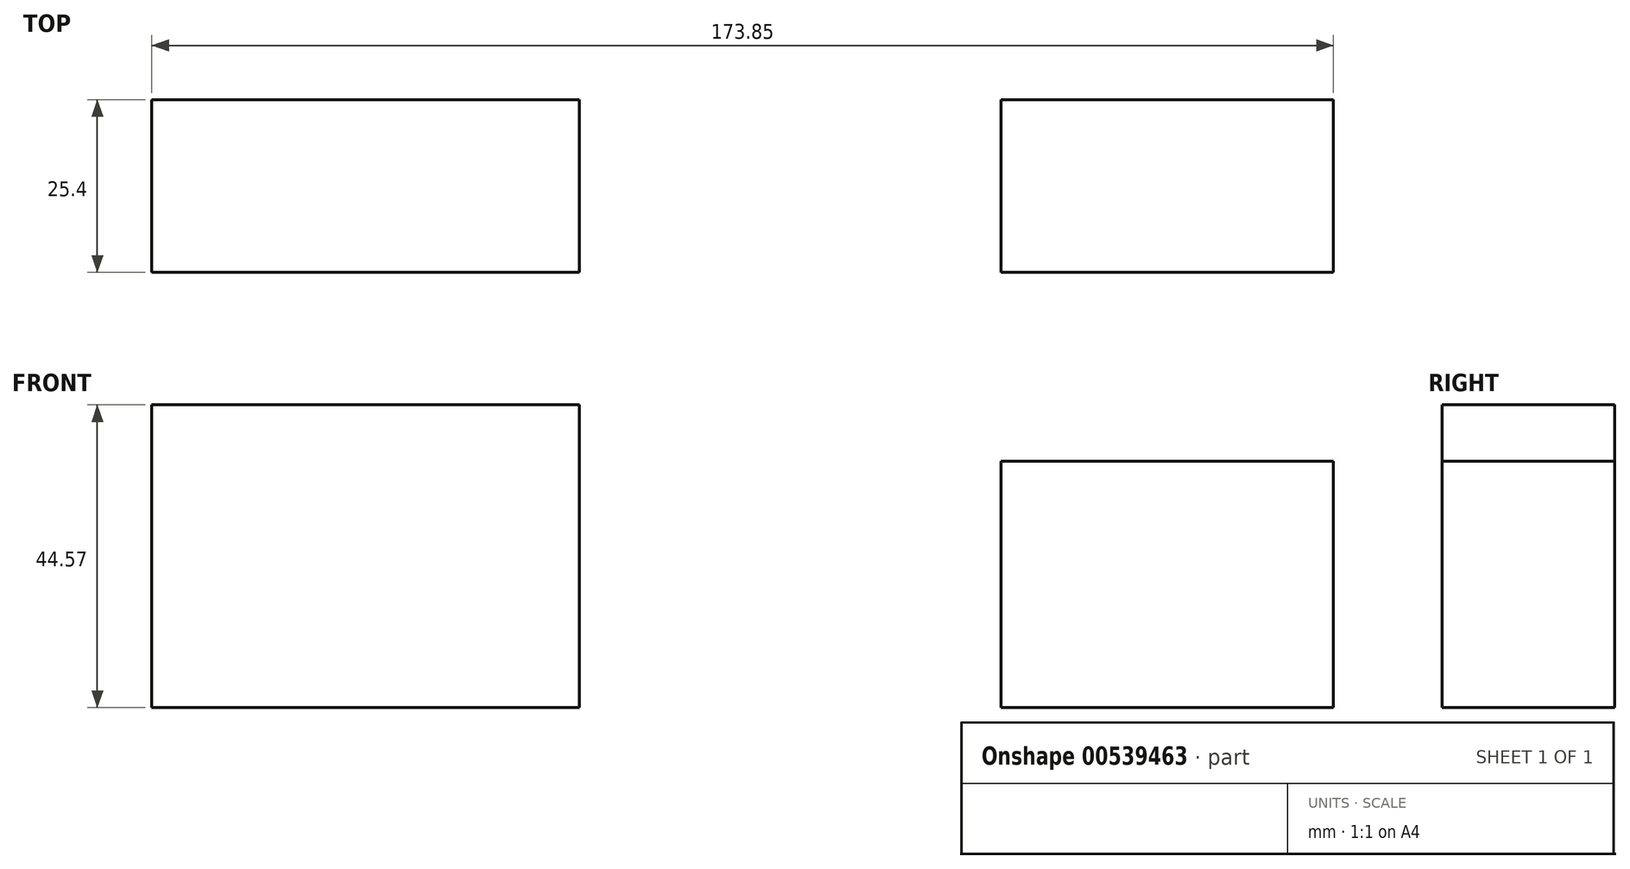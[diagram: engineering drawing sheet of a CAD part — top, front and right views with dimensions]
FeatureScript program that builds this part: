
annotation { "Feature Type Name" : "Feature", "Feature Type Description" : "" }
export const myFeature = defineFeature(function(context is Context, id is Id, definition is map)
    precondition{}
    {
        {
            var Q0;
            Q0=qCreatedBy(makeId("Front.planeOp"),FACE);
            var sketch = newSketch(context, id + "F0", { "sketchPlane" : qUnion([Q0])});
            skLineSegment(sketch, "E0.bottom", {"start": v(-92.4, 44.57) * mm, "end": v(-29.48, 44.57) * mm});
            skLineSegment(sketch, "E0.top", {"start": v(-92.4, 0) * mm, "end": v(-29.48, 0) * mm});
            skLineSegment(sketch, "E0.left", {"start": v(-92.4, 44.57) * mm, "end": v(-92.4, 0) * mm});
            skLineSegment(sketch, "E0.right", {"start": v(-29.48, 44.57) * mm, "end": v(-29.48, 0) * mm});
            skLineSegment(sketch, "E1.bottom", {"start": v(32.56, 36.24) * mm, "end": v(81.45, 36.24) * mm});
            skLineSegment(sketch, "E1.top", {"start": v(32.56, 0) * mm, "end": v(81.45, 0) * mm});
            skLineSegment(sketch, "E1.left", {"start": v(32.56, 36.24) * mm, "end": v(32.56, 0) * mm});
            skLineSegment(sketch, "E1.right", {"start": v(81.45, 36.24) * mm, "end": v(81.45, 0) * mm});
            skSolve(sketch);
        }
        {
            var Q0;
            Q0 = qSketchRegion(id + "F0", true);
            extrude(context, id + "F1", {"entities" : qUnion([Q0]), "depth" : 25.4 * mm, "offsetDistance" : 25.4 * mm});
        }
    });
